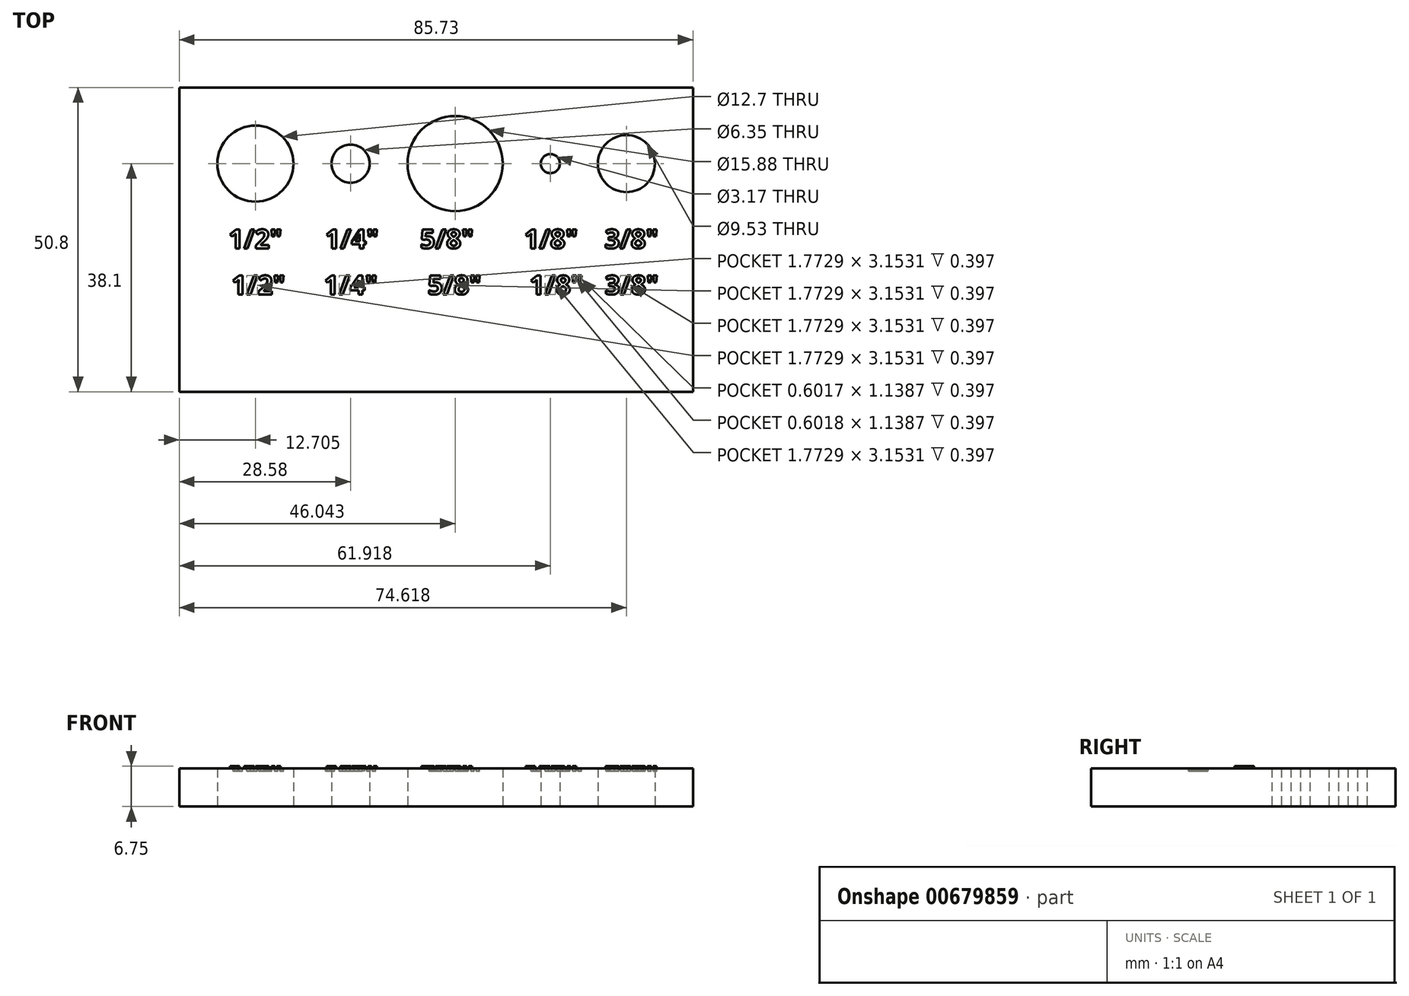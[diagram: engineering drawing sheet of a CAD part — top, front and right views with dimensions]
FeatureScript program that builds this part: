
annotation { "Feature Type Name" : "Feature", "Feature Type Description" : "" }
export const myFeature = defineFeature(function(context is Context, id is Id, definition is map)
    precondition{}
    {
        {
            var Q0;
            Q0=qCreatedBy(makeId("Top.planeOp"),FACE);
            var sketch = newSketch(context, id + "F0", { "sketchPlane" : qUnion([Q0])});
            skLineSegment(sketch, "E0.bottom", {"start": v(0, 0) * mm, "end": v(-85.72, 0) * mm});
            skLineSegment(sketch, "E0.top", {"start": v(0, 50.8) * mm, "end": v(-85.73, 50.8) * mm});
            skLineSegment(sketch, "E0.left", {"start": v(0, 0) * mm, "end": v(0, 50.8) * mm});
            skLineSegment(sketch, "E0.right", {"start": v(-85.72, 0) * mm, "end": v(-85.73, 50.8) * mm});
            skCircle(sketch, "E1", {"center": v(-73.03, 38.1) * mm, "radius": 6.35 * mm});
            skCircle(sketch, "E2", {"center": v(-57.15, 38.1) * mm, "radius": 3.18 * mm});
            skCircle(sketch, "E3", {"center": v(-39.69, 38.1) * mm, "radius": 7.94 * mm});
            skCircle(sketch, "E4", {"center": v(-23.81, 38.1) * mm, "radius": 1.59 * mm});
            skCircle(sketch, "E5", {"center": v(-11.11, 38.1) * mm, "radius": 4.76 * mm});
            skSolve(sketch);
        }
        {
            var Q0;
            Q0 = qSketchRegion(id + "F0", true);
            extrude(context, id + "F1", {"entities" : qUnion([Q0]), "depth" : 6.35 * mm, "offsetDistance" : 25.4 * mm});
        }
        {
            var Q0;
            Q0=makeQuery(id+"F1.opExtrude","CAP_FACE",FACE,{"disambiguationData":[OSD([sQuery(id+"F0.wireOp",EDGE,"E0.bottom"),sQuery(id+"F0.wireOp",EDGE,"E0.top"),sQuery(id+"F0.wireOp",EDGE,"E0.left"),sQuery(id+"F0.wireOp",EDGE,"E0.right"),sQuery(id+"F0.wireOp",EDGE,"E1"),sQuery(id+"F0.wireOp",EDGE,"E2"),sQuery(id+"F0.wireOp",EDGE,"E3"),sQuery(id+"F0.wireOp",EDGE,"E4"),sQuery(id+"F0.wireOp",EDGE,"E5")])],"isStart":false});
            var sketch = newSketch(context, id + "F2", { "sketchPlane" : qUnion([Q0])});
            skText(sketch, "E6", { "text": "1/2\"", "fontName": "OpenSans-Bold.ttf"});
            skText(sketch, "E7", { "text": "3/8\"", "fontName": "OpenSans-Bold.ttf"});
            skText(sketch, "E8", { "text": "5/8\"", "fontName": "OpenSans-Bold.ttf"});
            skText(sketch, "E9", { "text": "1/4\"", "fontName": "OpenSans-Bold.ttf"});
            skText(sketch, "E10", { "text": "1/8\"", "fontName": "OpenSans-Bold.ttf"});
            const initialGuessF2  = {"E6": [-0.0775, 0.02395, 1, 0, 0.00318], "E7": [-0.01474, 0.02395, 1, 0, 0.00318], "E8": [-0.04554, 0.02395, 1, 0, 0.00318], "E9": [-0.0614, 0.02395, 1, 0, 0.00318], "E10": [-0.02818, 0.02395, 1, 0, 0.00318]};
            skSetInitialGuess(sketch, initialGuessF2);
            skSolve(sketch);
        }
        {
            var Q0;
            Q0=makeQuery(id+"F2.imprint","IMPRINT",FACE,{"disambiguationData":[TD([[makeQuery(id+"F2.imprint","IMPRINT",EDGE,{"derivedFrom":sQuery(id+"F2.wireOp",EDGE,"E6.sketch_text.stroke-0")}),1.0]])]});
            var sketch = newSketch(context, id + "F3", { "sketchPlane" : qUnion([Q0])});
            skText(sketch, "E11", { "text": "1/2\"", "fontName": "OpenSans-Bold.ttf"});
            skText(sketch, "E12", { "text": "3/8\"", "fontName": "OpenSans-Bold.ttf"});
            skText(sketch, "E13", { "text": "5/8\"", "fontName": "OpenSans-Bold.ttf"});
            skText(sketch, "E14", { "text": "1/4\"", "fontName": "OpenSans-Bold.ttf"});
            skText(sketch, "E15", { "text": "1/8\"", "fontName": "OpenSans-Bold.ttf"});
            const initialGuessF3  = {"E11": [-0.077, 0.01626, 1, 0, 0.00318], "E12": [-0.0147, 0.01626, 1, 0, 0.00318], "E13": [-0.04425, 0.01626, 1, 0, 0.00318], "E14": [-0.0616, 0.01626, 1, 0, 0.00318], "E15": [-0.02727, 0.01626, 1, 0, 0.00318]};
            skSetInitialGuess(sketch, initialGuessF3);
            skSolve(sketch);
        }
        {
            var Q0;
            Q0 = qSketchRegion(id + "F2", true);
            extrude(context, id + "F4", {"entities" : qUnion([Q0]), "operationType" : NewBodyOperationType.ADD, "flatOperationType" : FlatOperationType.REMOVE, "depth" : 0.4 * mm, "offsetDistance" : 25.4 * mm, "domain" : OperationDomain.MODEL});
        }
        {
            var Q0;
            Q0 = qSketchRegion(id + "F3", true);
            extrude(context, id + "F5", {"entities" : qUnion([Q0]), "operationType" : NewBodyOperationType.REMOVE, "oppositeDirection" : true, "depth" : 0.4 * mm, "offsetDistance" : 25.4 * mm});
        }
    });
